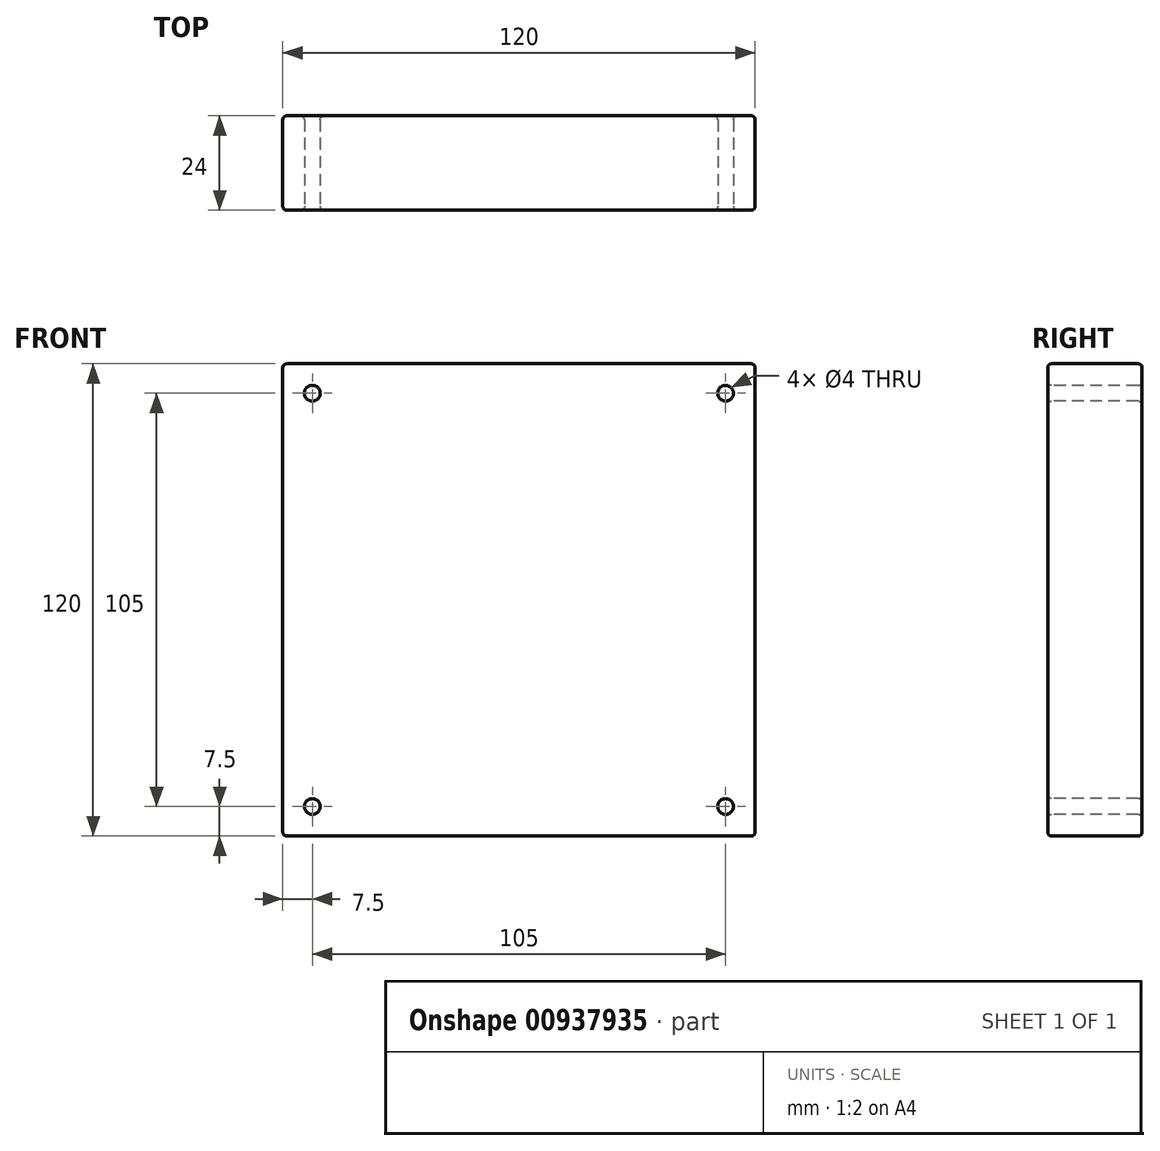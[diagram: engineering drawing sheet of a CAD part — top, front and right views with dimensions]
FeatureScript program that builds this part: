
annotation { "Feature Type Name" : "Feature", "Feature Type Description" : "" }
export const myFeature = defineFeature(function(context is Context, id is Id, definition is map)
    precondition{}
    {
        {
            var Q0;
            Q0=qCreatedBy(makeId("Front.planeOp"),FACE);
            var sketch = newSketch(context, id + "F0", { "sketchPlane" : qUnion([Q0])});
            skLineSegment(sketch, "E0.bottom", {"start": v(60, -60) * mm, "end": v(-60, -60) * mm});
            skLineSegment(sketch, "E0.top", {"start": v(60, 60) * mm, "end": v(-60, 60) * mm});
            skLineSegment(sketch, "E0.left", {"start": v(60, -60) * mm, "end": v(60, 60) * mm});
            skLineSegment(sketch, "E0.right", {"start": v(-60, -60) * mm, "end": v(-60, 60) * mm});
            skPoint(sketch, "E0.middle", {"position": v(0, 0) * mm});
            skSolve(sketch);
        }
        {
            var Q0;
            Q0=makeQuery(id+"F0.imprint","IMPRINT",FACE,{"disambiguationData":[TD([[makeQuery(id+"F0.imprint","IMPRINT",EDGE,{"derivedFrom":sQuery(id+"F0.wireOp",EDGE,"E0.bottom")}),-1.0]])]});
            extrude(context, id + "F1", {"entities" : qUnion([Q0]), "depth" : 24 * mm, "offsetDistance" : 25 * mm});
        }
        {
            var Q0;
            Q0=makeQuery(id+"F1.opExtrude","CAP_FACE",FACE,{"disambiguationData":[OSD([sQuery(id+"F0.wireOp",EDGE,"E0.bottom"),sQuery(id+"F0.wireOp",EDGE,"E0.top"),sQuery(id+"F0.wireOp",EDGE,"E0.left"),sQuery(id+"F0.wireOp",EDGE,"E0.right")])],"isStart":false});
            var sketch = newSketch(context, id + "F2", { "sketchPlane" : qUnion([Q0])});
            skPoint(sketch, "E1", {"position": v(-52.5, 52.5) * mm});
            skPoint(sketch, "E2", {"position": v(52.5, 52.5) * mm});
            skPoint(sketch, "E3", {"position": v(52.5, -52.5) * mm});
            skPoint(sketch, "E4", {"position": v(-52.5, -52.5) * mm});
            skSolve(sketch);
        }
        {
            var Q0;
            Q0=sQuery(id+"F2.wireOp",VERTEX,"E1");
            var Q1;
            Q1=sQuery(id+"F2.wireOp",VERTEX,"E2");
            var Q2;
            Q2=sQuery(id+"F2.wireOp",VERTEX,"E3");
            var Q3;
            Q3=sQuery(id+"F2.wireOp",VERTEX,"E4");
            var Q4;
            Q4=makeQuery(id+"F1.opExtrude","SWEPT_BODY",BODY,{"disambiguationData":[OSD([sQuery(id+"F0.wireOp",EDGE,"E0.bottom"),sQuery(id+"F0.wireOp",EDGE,"E0.top"),sQuery(id+"F0.wireOp",EDGE,"E0.left"),sQuery(id+"F0.wireOp",EDGE,"E0.right")])]});
            hole(context, id + "F3", {"style" : HoleStyle.SIMPLE, "endStyle" : HoleEndStyle.THROUGH, "holeDiameter" : 4 * mm, "majorDiameter" : 5 * mm, "isTappedThrough" : true, "tappedDepth" : 12 * mm, "tapClearance" : 3, "startFromSketch" : true, "locations" : qUnion([Q0, Q1, Q2, Q3]), "scope" : qUnion([Q4])});
        }
        {
            var Q0;
            Q0=makeQuery(id+"F1.opExtrude","SWEPT_FACE",FACE,{"disambiguationData":[OSD([sQuery(id+"F0.wireOp",EDGE,"E0.top")])]});
            var Q1;
            Q1=makeQuery(id+"F1.opExtrude","CAP_FACE",FACE,{"disambiguationData":[OSD([sQuery(id+"F0.wireOp",EDGE,"E0.bottom"),sQuery(id+"F0.wireOp",EDGE,"E0.top"),sQuery(id+"F0.wireOp",EDGE,"E0.left"),sQuery(id+"F0.wireOp",EDGE,"E0.right")])],"isStart":false});
            var Q2;
            Q2=makeQuery(id+"F1.opExtrude","SWEPT_FACE",FACE,{"disambiguationData":[OSD([sQuery(id+"F0.wireOp",EDGE,"E0.left")])]});
            var Q3;
            Q3=makeQuery(id+"F1.opExtrude","CAP_FACE",FACE,{"disambiguationData":[OSD([sQuery(id+"F0.wireOp",EDGE,"E0.bottom"),sQuery(id+"F0.wireOp",EDGE,"E0.top"),sQuery(id+"F0.wireOp",EDGE,"E0.left"),sQuery(id+"F0.wireOp",EDGE,"E0.right")])],"isStart":true});
            var Q4;
            Q4=makeQuery(id+"F1.opExtrude","SWEPT_FACE",FACE,{"disambiguationData":[OSD([sQuery(id+"F0.wireOp",EDGE,"E0.right")])]});
            var Q5;
            Q5=makeQuery(id+"F1.opExtrude","SWEPT_FACE",FACE,{"disambiguationData":[OSD([sQuery(id+"F0.wireOp",EDGE,"E0.bottom")])]});
            fillet(context, id + "F4", {"entities" : qUnion([Q0, Q1, Q2, Q3, Q4, Q5]), "radius" : 1 * mm, "tangentPropagation" : true, "allowEdgeOverflow" : false});
        }
    });
